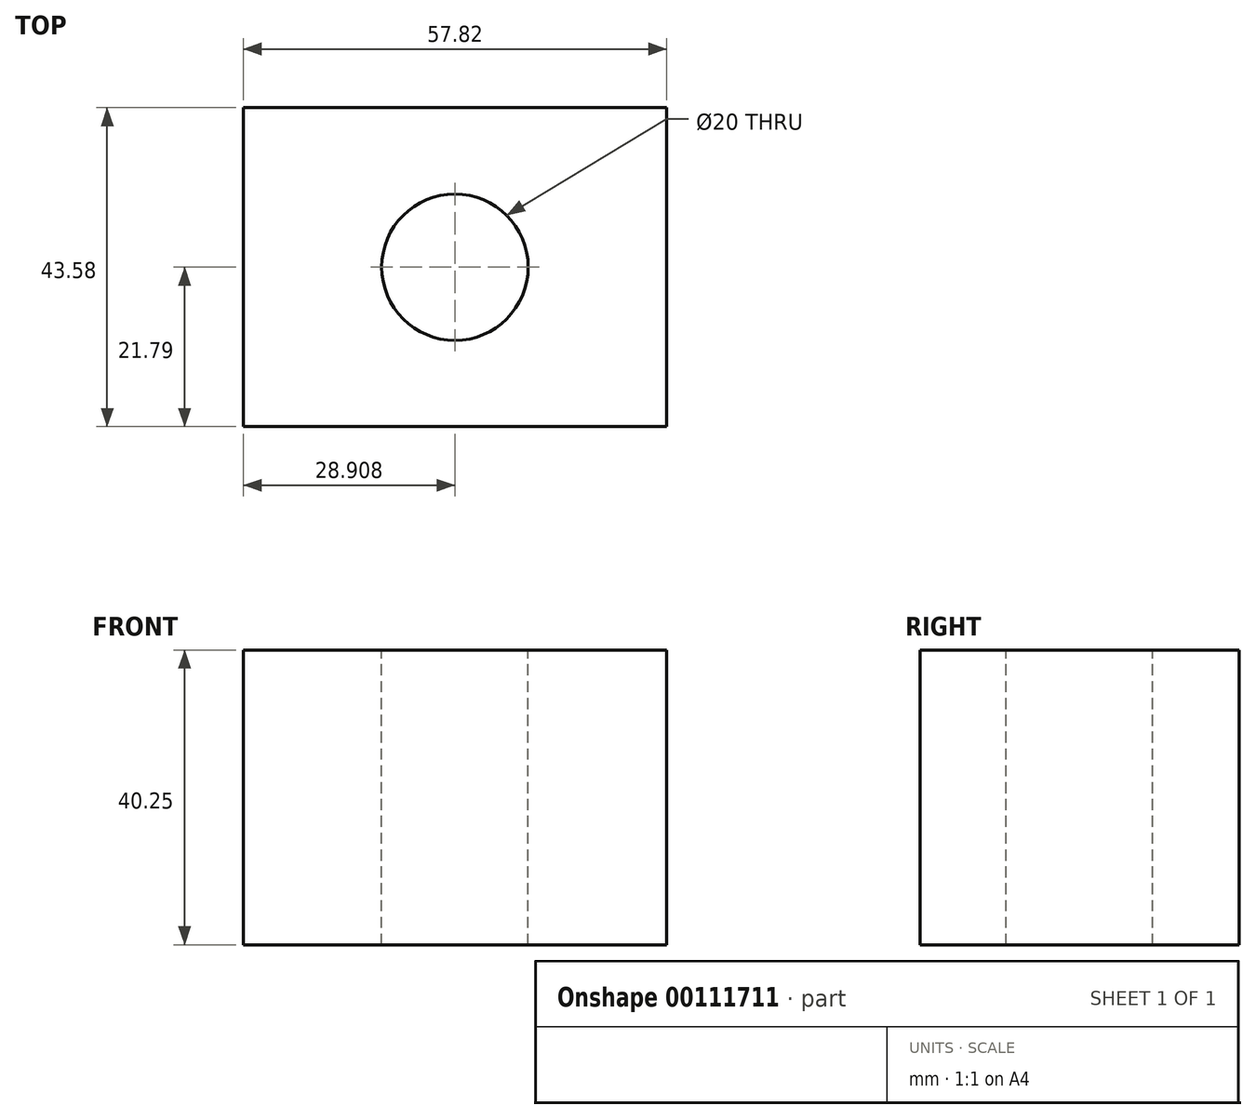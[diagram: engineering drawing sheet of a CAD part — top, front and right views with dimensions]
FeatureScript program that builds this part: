
annotation { "Feature Type Name" : "Feature", "Feature Type Description" : "" }
export const myFeature = defineFeature(function(context is Context, id is Id, definition is map)
    precondition{}
    {
        {
            var Q0;
            Q0=qCreatedBy(makeId("Front.planeOp"),FACE);
            var sketch = newSketch(context, id + "F0", { "sketchPlane" : qUnion([Q0])});
            skLineSegment(sketch, "E0.bottom", {"start": v(0, 0) * mm, "end": v(57.82, 0) * mm});
            skLineSegment(sketch, "E0.top", {"start": v(0, 40.25) * mm, "end": v(57.82, 40.25) * mm});
            skLineSegment(sketch, "E0.left", {"start": v(0, 0) * mm, "end": v(0, 40.25) * mm});
            skLineSegment(sketch, "E0.right", {"start": v(57.82, 0) * mm, "end": v(57.82, 40.25) * mm});
            skSolve(sketch);
        }
        {
            var Q0;
            Q0=makeQuery(id+"F0.imprint","IMPRINT",FACE,{"disambiguationData":[TD([[makeQuery(id+"F0.imprint","IMPRINT",EDGE,{"derivedFrom":sQuery(id+"F0.wireOp",EDGE,"E0.bottom")}),1.0]])]});
            extrude(context, id + "F1", {"entities" : qUnion([Q0]), "depth" : 43.58 * mm});
        }
        {
            var Q0;
            Q0=makeQuery(id+"F1.opExtrude","SWEPT_FACE",FACE,{"disambiguationData":[OSD([sQuery(id+"F0.wireOp",EDGE,"E0.top")])]});
            var sketch = newSketch(context, id + "F2", { "sketchPlane" : qUnion([Q0])});
            skCircle(sketch, "E1", {"center": v(28.9, -21.79) * mm, "radius": 10.97 * mm});
            skPoint(sketch, "E1.centerSnap0", {"position": v(28.9, 0) * mm});
            skPoint(sketch, "E1.centerSnap1", {"position": v(0, -21.79) * mm});
            skSolve(sketch);
        }
        {
            var Q0;
            Q0=sQuery(id+"F2.wireOp",VERTEX,"E1.center");
            var Q1;
            Q1=makeQuery(id+"F1.opExtrude","SWEPT_BODY",BODY,{"disambiguationData":[OSD([sQuery(id+"F0.wireOp",EDGE,"E0.bottom"),sQuery(id+"F0.wireOp",EDGE,"E0.top"),sQuery(id+"F0.wireOp",EDGE,"E0.left"),sQuery(id+"F0.wireOp",EDGE,"E0.right")])]});
            hole(context, id + "F3", {"style" : HoleStyle.SIMPLE, "endStyle" : HoleEndStyle.THROUGH, "holeDiameter" : 20 * mm, "locations" : qUnion([Q0]), "scope" : qUnion([Q1]), "isTappedThrough" : true});
        }
    });
